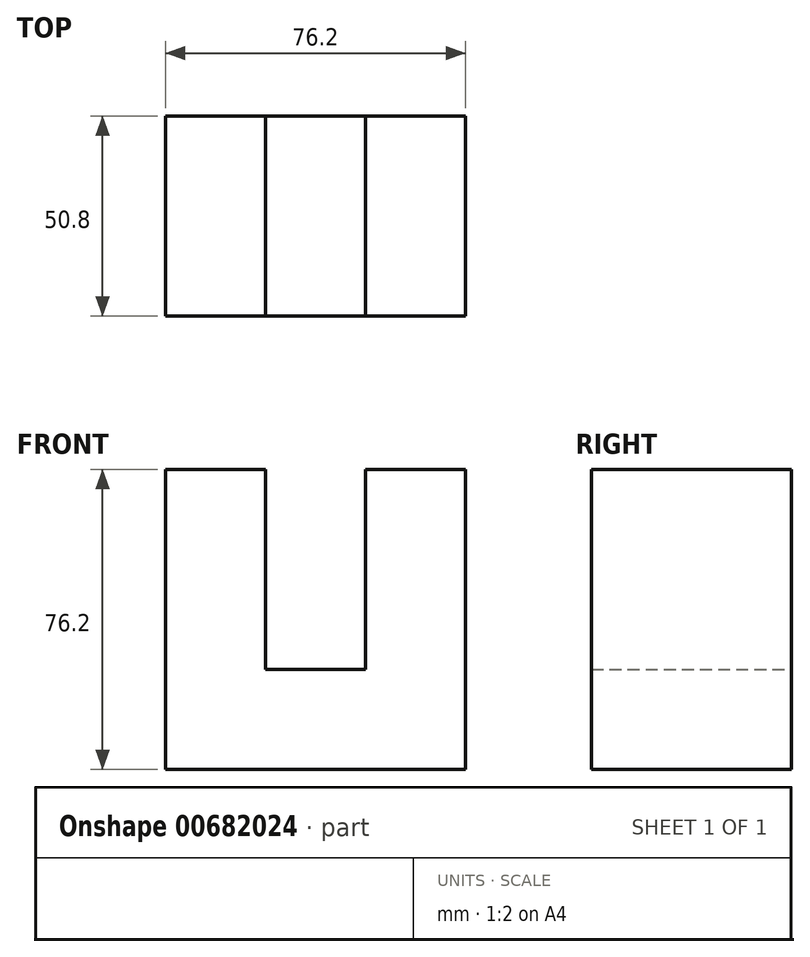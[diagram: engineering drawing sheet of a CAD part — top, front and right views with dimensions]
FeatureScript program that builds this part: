
annotation { "Feature Type Name" : "Feature", "Feature Type Description" : "" }
export const myFeature = defineFeature(function(context is Context, id is Id, definition is map)
    precondition{}
    {
        {
            var Q0;
            Q0=qCreatedBy(makeId("Front.planeOp"),FACE);
            var sketch = newSketch(context, id + "F0", { "sketchPlane" : qUnion([Q0])});
            skLineSegment(sketch, "E0", {"start": v(-12.33, 80.85) * mm, "end": v(-37.73, 80.85) * mm});
            skLineSegment(sketch, "E1", {"start": v(-37.73, 80.85) * mm, "end": v(-37.73, 4.65) * mm});
            skLineSegment(sketch, "E2", {"start": v(-37.73, 4.65) * mm, "end": v(38.47, 4.65) * mm});
            skLineSegment(sketch, "E3", {"start": v(38.47, 4.65) * mm, "end": v(38.47, 80.85) * mm});
            skLineSegment(sketch, "E4", {"start": v(38.47, 80.85) * mm, "end": v(13.07, 80.85) * mm});
            skLineSegment(sketch, "E5", {"start": v(13.07, 80.85) * mm, "end": v(13.07, 30.05) * mm});
            skLineSegment(sketch, "E6", {"start": v(13.07, 30.05) * mm, "end": v(-12.33, 30.05) * mm});
            skLineSegment(sketch, "E7", {"start": v(-12.33, 30.05) * mm, "end": v(-12.33, 80.85) * mm});
            skSolve(sketch);
        }
        {
            var Q0;
            Q0 = qSketchRegion(id + "F0", true);
            extrude(context, id + "F1", {"entities" : qUnion([Q0]), "depth" : 50.8 * mm, "offsetDistance" : 25.4 * mm});
        }
    });
